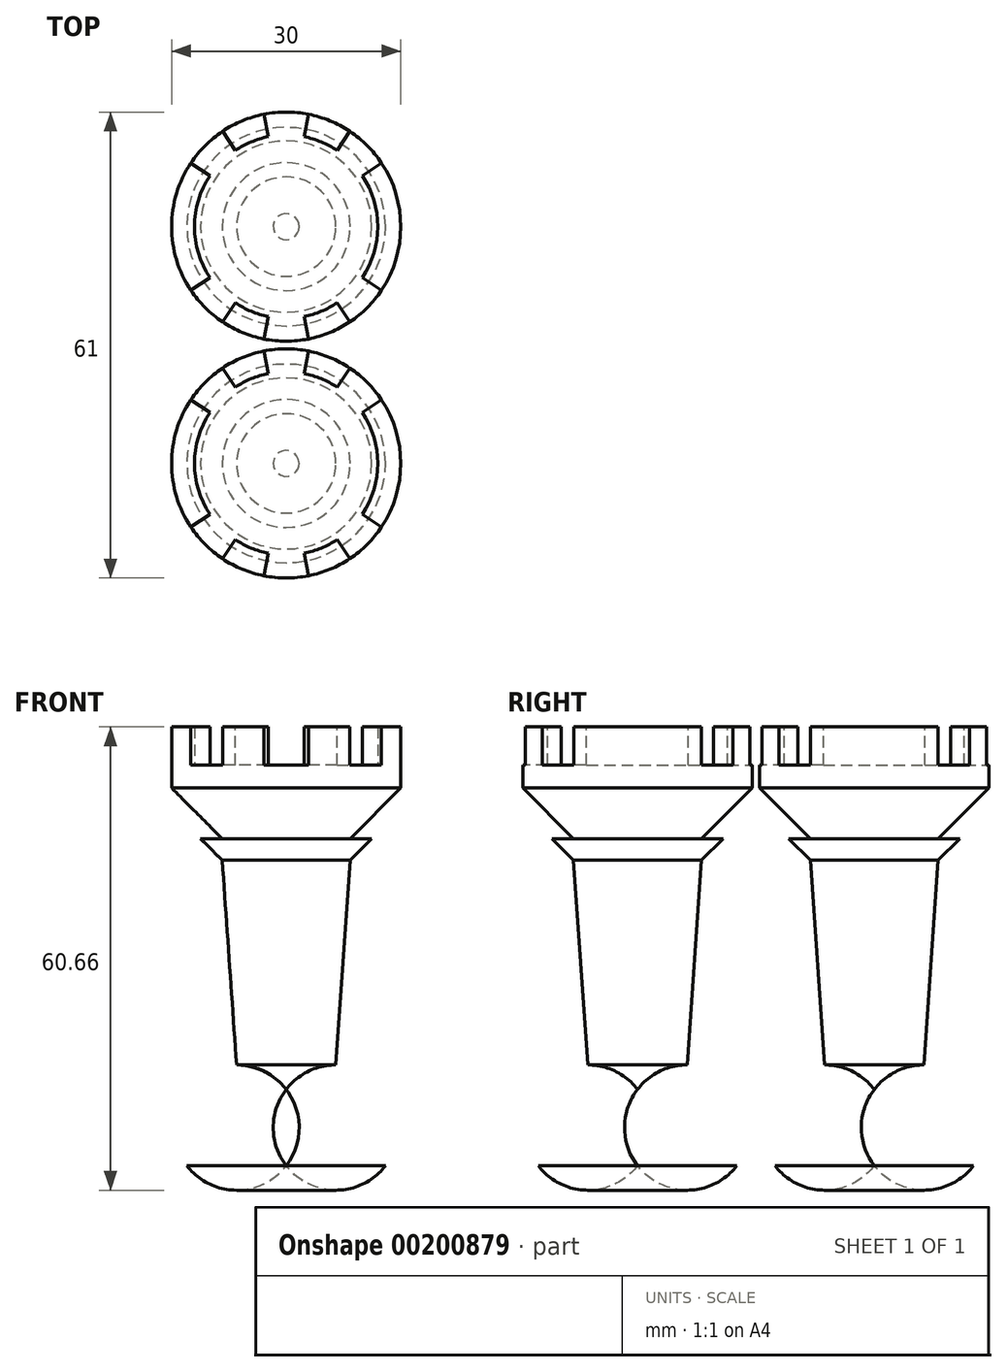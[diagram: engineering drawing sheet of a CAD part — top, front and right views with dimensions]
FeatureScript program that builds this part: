
annotation { "Feature Type Name" : "Feature", "Feature Type Description" : "" }
export const myFeature = defineFeature(function(context is Context, id is Id, definition is map)
    precondition{}
    {
        {
            var Q0;
            Q0=qCreatedBy(makeId("Front.planeOp"),FACE);
            var sketch = newSketch(context, id + "F0", { "sketchPlane" : qUnion([Q0])});
            skLineSegment(sketch, "E0", {"start": v(-1.52, -33.92) * mm, "end": v(-14.52, -33.92) * mm});
            skArc(sketch, "E1", {"start": v(-14.52, -33.92) * mm, "mid": v(-15.38, -25.3) * mm, "end": v(-8.02, -20.72) * mm});
            skPoint(sketch, "E1.centerSnap0", {"position": v(-8.02, -33.92) * mm});
            skLineSegment(sketch, "E2", {"start": v(-1.52, -33.92) * mm, "end": v(-1.52, 32.35) * mm});
            skLineSegment(sketch, "E3", {"start": v(-8.02, -20.72) * mm, "end": v(-9.9, 6.08) * mm});
            skLineSegment(sketch, "E4", {"start": v(-9.9, 6.08) * mm, "end": v(-12.73, 8.91) * mm});
            skLineSegment(sketch, "E5", {"start": v(-12.73, 8.91) * mm, "end": v(-9.9, 8.91) * mm});
            skPoint(sketch, "E6.orphan", {"position": v(-1.52, 29.85) * mm});
            skPoint(sketch, "E7.MirrorCS.start.orphan", {"position": v(6.85, 8.91) * mm});
            skPoint(sketch, "E8.MirrorCS.start.orphan", {"position": v(9.68, 8.91) * mm});
            skPoint(sketch, "E9.MirrorCS.start.orphan", {"position": v(6.85, 6.08) * mm});
            skPoint(sketch, "E10.MirrorCS.start.orphan", {"position": v(4.98, -20.72) * mm});
            skPoint(sketch, "E11.MirrorCS.start.orphan", {"position": v(11.48, -33.92) * mm});
            skPoint(sketch, "E12.orphan", {"position": v(-1.52, 36.08) * mm});
            skLineSegment(sketch, "E13", {"start": v(-9.9, 8.91) * mm, "end": v(-16.52, 15.54) * mm});
            skLineSegment(sketch, "E14", {"start": v(-16.52, 15.54) * mm, "end": v(-16.52, 23.54) * mm});
            skLineSegment(sketch, "E15", {"start": v(-16.52, 23.54) * mm, "end": v(-13.52, 23.54) * mm});
            skLineSegment(sketch, "E16", {"start": v(-13.52, 23.54) * mm, "end": v(-13.52, 18.54) * mm});
            skLineSegment(sketch, "E17", {"start": v(-13.52, 18.54) * mm, "end": v(-1.52, 18.54) * mm});
            skSolve(sketch);
        }
        {
            var Q0;
            {var subQ0=sQuery(id+"F0.wireOp",EDGE,"E0");Q0=makeQuery(id+"F0.imprint","IMPRINT",FACE,{"disambiguationData":[TD([[makeQuery(id+"F0.imprint","IMPRINT",EDGE,{"derivedFrom":subQ0}),-1.0]])]});}
            var Q1;
            Q1=sQuery(id+"F0.wireOp",EDGE,"E2");
            revolve(context, id + "F1", {"entities" : qUnion([Q0]), "axis" : qUnion([Q1]), "revolveType" : RevolveType.FULL});
        }
        {
            var Q0;
            Q0=makeQuery(id+"F1.opRevolve","SWEPT_FACE",FACE,{"disambiguationData":[OSD([sQuery(id+"F0.wireOp",EDGE,"E15")])]});
            var sketch = newSketch(context, id + "F2", { "sketchPlane" : qUnion([Q0])});
            skLineSegment(sketch, "E18", {"start": v(-16.52, 0) * mm, "end": v(13.48, 0) * mm});
            skPoint(sketch, "E19", {"position": v(-1.52, 0) * mm});
            skLineSegment(sketch, "E20", {"start": v(-16.24, 2.93) * mm, "end": v(-1.52, 0) * mm});
            skLineSegment(sketch, "E21", {"start": v(-1.52, 0) * mm, "end": v(13.19, -2.93) * mm});
            skLineSegment(sketch, "E22.MirrorCS", {"start": v(-16.24, -2.93) * mm, "end": v(-1.52, 0) * mm});
            skLineSegment(sketch, "E23.MirrorCS", {"start": v(-1.52, 0) * mm, "end": v(13.19, 2.93) * mm});
            skLineSegment(sketch, "E24", {"start": v(-1.52, 0) * mm, "end": v(-14, 8.33) * mm});
            skLineSegment(sketch, "E25", {"start": v(-1.52, 0) * mm, "end": v(-9.86, 12.47) * mm});
            skLineSegment(sketch, "E26", {"start": v(-1.52, 0) * mm, "end": v(-4.45, 14.71) * mm});
            skLineSegment(sketch, "E27", {"start": v(-1.52, 0) * mm, "end": v(1.4, 14.71) * mm});
            skLineSegment(sketch, "E28", {"start": v(-1.52, 0) * mm, "end": v(6.8, 12.47) * mm});
            skLineSegment(sketch, "E29", {"start": v(-1.52, 0) * mm, "end": v(10.95, 8.33) * mm});
            skLineSegment(sketch, "E30.MirrorCS", {"start": v(-1.52, 0) * mm, "end": v(-14, -8.33) * mm});
            skLineSegment(sketch, "E31.MirrorCS", {"start": v(-1.52, 0) * mm, "end": v(-9.86, -12.47) * mm});
            skLineSegment(sketch, "E32.MirrorCS", {"start": v(-1.52, 0) * mm, "end": v(-4.45, -14.71) * mm});
            skLineSegment(sketch, "E33.MirrorCS", {"start": v(-1.52, 0) * mm, "end": v(1.4, -14.71) * mm});
            skLineSegment(sketch, "E34.MirrorCS", {"start": v(-1.52, 0) * mm, "end": v(6.8, -12.47) * mm});
            skLineSegment(sketch, "E35.MirrorCS", {"start": v(-1.52, 0) * mm, "end": v(10.95, -8.33) * mm});
            skSolve(sketch);
        }
        {
            var Q0;
            {var subQ0=sQuery(id+"F2.wireOp",EDGE,"E18");var subQ1=sQuery(id+"F0.wireOp",EDGE,"E15");var subQ2=makeQuery(id+"F1.opRevolve","SWEPT_EDGE",EDGE,{"disambiguationData":[OSD([sQuery(id+"F0.wireOp",EDGE,"E14"),subQ1])]});var subQ3=makeQuery(id+"F2.imprint","INTERSECT",VERTEX,{"disambiguationData":[OD(0.0)],"derivedFrom":[subQ2,subQ0]});Q0=makeQuery(id+"F2.imprint","IMPRINT",FACE,{"disambiguationData":[TD([[makeQuery(id+"F2.imprint","IMPRINT",EDGE,{"disambiguationData":[TD([[subQ3,-1.0]])],"derivedFrom":subQ0}),-1.0]])]});}
            var Q1;
            {var subQ0=sQuery(id+"F2.wireOp",EDGE,"E18");var subQ1=sQuery(id+"F0.wireOp",EDGE,"E15");var subQ2=makeQuery(id+"F1.opRevolve","SWEPT_EDGE",EDGE,{"disambiguationData":[OSD([sQuery(id+"F0.wireOp",EDGE,"E14"),subQ1])]});var subQ3=makeQuery(id+"F2.imprint","INTERSECT",VERTEX,{"disambiguationData":[OD(0.0)],"derivedFrom":[subQ2,subQ0]});Q1=makeQuery(id+"F2.imprint","IMPRINT",FACE,{"disambiguationData":[TD([[makeQuery(id+"F2.imprint","IMPRINT",EDGE,{"disambiguationData":[TD([[subQ3,-1.0]])],"derivedFrom":subQ0}),1.0]])]});}
            var Q2;
            {var subQ0=sQuery(id+"F2.wireOp",EDGE,"E24");var subQ1=sQuery(id+"F0.wireOp",EDGE,"E15");var subQ2=makeQuery(id+"F1.opRevolve","SWEPT_EDGE",EDGE,{"disambiguationData":[OSD([sQuery(id+"F0.wireOp",EDGE,"E14"),subQ1])]});var subQ3=makeQuery(id+"F2.imprint","INTERSECT",VERTEX,{"derivedFrom":[subQ2,subQ0]});Q2=makeQuery(id+"F2.imprint","IMPRINT",FACE,{"disambiguationData":[TD([[makeQuery(id+"F2.imprint","IMPRINT",EDGE,{"disambiguationData":[TD([[subQ3,1.0]])],"derivedFrom":subQ0}),-1.0]])]});}
            var Q3;
            {var subQ0=sQuery(id+"F2.wireOp",EDGE,"E26");var subQ1=sQuery(id+"F0.wireOp",EDGE,"E15");var subQ2=makeQuery(id+"F1.opRevolve","SWEPT_EDGE",EDGE,{"disambiguationData":[OSD([sQuery(id+"F0.wireOp",EDGE,"E14"),subQ1])]});var subQ3=makeQuery(id+"F2.imprint","INTERSECT",VERTEX,{"derivedFrom":[subQ2,subQ0]});Q3=makeQuery(id+"F2.imprint","IMPRINT",FACE,{"disambiguationData":[TD([[makeQuery(id+"F2.imprint","IMPRINT",EDGE,{"disambiguationData":[TD([[subQ3,1.0]])],"derivedFrom":subQ0}),-1.0]])]});}
            var Q4;
            {var subQ0=sQuery(id+"F2.wireOp",EDGE,"E28");var subQ1=sQuery(id+"F0.wireOp",EDGE,"E15");var subQ2=makeQuery(id+"F1.opRevolve","SWEPT_EDGE",EDGE,{"disambiguationData":[OSD([sQuery(id+"F0.wireOp",EDGE,"E14"),subQ1])]});var subQ3=makeQuery(id+"F2.imprint","INTERSECT",VERTEX,{"derivedFrom":[subQ2,subQ0]});Q4=makeQuery(id+"F2.imprint","IMPRINT",FACE,{"disambiguationData":[TD([[makeQuery(id+"F2.imprint","IMPRINT",EDGE,{"disambiguationData":[TD([[subQ3,1.0]])],"derivedFrom":subQ0}),-1.0]])]});}
            var Q5;
            {var subQ0=sQuery(id+"F2.wireOp",EDGE,"E18");var subQ1=sQuery(id+"F0.wireOp",EDGE,"E15");var subQ2=makeQuery(id+"F1.opRevolve","SWEPT_EDGE",EDGE,{"disambiguationData":[OSD([sQuery(id+"F0.wireOp",EDGE,"E14"),subQ1])]});var subQ3=makeQuery(id+"F2.imprint","INTERSECT",VERTEX,{"disambiguationData":[OD(1.0)],"derivedFrom":[subQ2,subQ0]});Q5=makeQuery(id+"F2.imprint","IMPRINT",FACE,{"disambiguationData":[TD([[makeQuery(id+"F2.imprint","IMPRINT",EDGE,{"disambiguationData":[TD([[subQ3,1.0]])],"derivedFrom":subQ0}),1.0]])]});}
            var Q6;
            {var subQ0=sQuery(id+"F2.wireOp",EDGE,"E18");var subQ1=sQuery(id+"F0.wireOp",EDGE,"E15");var subQ2=makeQuery(id+"F1.opRevolve","SWEPT_EDGE",EDGE,{"disambiguationData":[OSD([sQuery(id+"F0.wireOp",EDGE,"E14"),subQ1])]});var subQ3=makeQuery(id+"F2.imprint","INTERSECT",VERTEX,{"disambiguationData":[OD(1.0)],"derivedFrom":[subQ2,subQ0]});Q6=makeQuery(id+"F2.imprint","IMPRINT",FACE,{"disambiguationData":[TD([[makeQuery(id+"F2.imprint","IMPRINT",EDGE,{"disambiguationData":[TD([[subQ3,1.0]])],"derivedFrom":subQ0}),-1.0]])]});}
            var Q7;
            {var subQ0=sQuery(id+"F2.wireOp",EDGE,"E34.MirrorCS");var subQ1=sQuery(id+"F0.wireOp",EDGE,"E15");var subQ2=makeQuery(id+"F1.opRevolve","SWEPT_EDGE",EDGE,{"disambiguationData":[OSD([sQuery(id+"F0.wireOp",EDGE,"E14"),subQ1])]});var subQ3=makeQuery(id+"F2.imprint","INTERSECT",VERTEX,{"derivedFrom":[subQ2,subQ0]});Q7=makeQuery(id+"F2.imprint","IMPRINT",FACE,{"disambiguationData":[TD([[makeQuery(id+"F2.imprint","IMPRINT",EDGE,{"disambiguationData":[TD([[subQ3,1.0]])],"derivedFrom":subQ0}),1.0]])]});}
            var Q8;
            {var subQ0=sQuery(id+"F2.wireOp",EDGE,"E32.MirrorCS");var subQ1=sQuery(id+"F0.wireOp",EDGE,"E15");var subQ2=makeQuery(id+"F1.opRevolve","SWEPT_EDGE",EDGE,{"disambiguationData":[OSD([sQuery(id+"F0.wireOp",EDGE,"E14"),subQ1])]});var subQ3=makeQuery(id+"F2.imprint","INTERSECT",VERTEX,{"derivedFrom":[subQ2,subQ0]});Q8=makeQuery(id+"F2.imprint","IMPRINT",FACE,{"disambiguationData":[TD([[makeQuery(id+"F2.imprint","IMPRINT",EDGE,{"disambiguationData":[TD([[subQ3,1.0]])],"derivedFrom":subQ0}),1.0]])]});}
            var Q9;
            {var subQ0=sQuery(id+"F2.wireOp",EDGE,"E30.MirrorCS");var subQ1=sQuery(id+"F0.wireOp",EDGE,"E15");var subQ2=makeQuery(id+"F1.opRevolve","SWEPT_EDGE",EDGE,{"disambiguationData":[OSD([sQuery(id+"F0.wireOp",EDGE,"E14"),subQ1])]});var subQ3=makeQuery(id+"F2.imprint","INTERSECT",VERTEX,{"derivedFrom":[subQ2,subQ0]});Q9=makeQuery(id+"F2.imprint","IMPRINT",FACE,{"disambiguationData":[TD([[makeQuery(id+"F2.imprint","IMPRINT",EDGE,{"disambiguationData":[TD([[subQ3,1.0]])],"derivedFrom":subQ0}),1.0]])]});}
            extrude(context, id + "F3", {"entities" : qUnion([Q0, Q1, Q2, Q3, Q4, Q5, Q6, Q7, Q8, Q9]), "operationType" : NewBodyOperationType.REMOVE, "oppositeDirection" : true, "depth" : 5 * mm});
        }
        {
            var Q0;
            Q0=makeQuery(id+"F1.opRevolve","SWEPT_BODY",BODY,{"disambiguationData":[OSD([sQuery(id+"F0.wireOp",EDGE,"E0"),sQuery(id+"F0.wireOp",EDGE,"E1"),sQuery(id+"F0.wireOp",EDGE,"E2"),sQuery(id+"F0.wireOp",EDGE,"E3"),sQuery(id+"F0.wireOp",EDGE,"E4"),sQuery(id+"F0.wireOp",EDGE,"E5"),sQuery(id+"F0.wireOp",EDGE,"E13"),sQuery(id+"F0.wireOp",EDGE,"E14"),sQuery(id+"F0.wireOp",EDGE,"E15"),sQuery(id+"F0.wireOp",EDGE,"E16"),sQuery(id+"F0.wireOp",EDGE,"E17")])]});
            transform(context, id + "F4", {"entities" : qUnion([Q0]), "transformType" : TransformType.TRANSLATION_3D, "dx" : 0 * mm, "dy" : 31 * mm, "dz" : 0 * mm, "makeCopy" : true});
        }
    });
